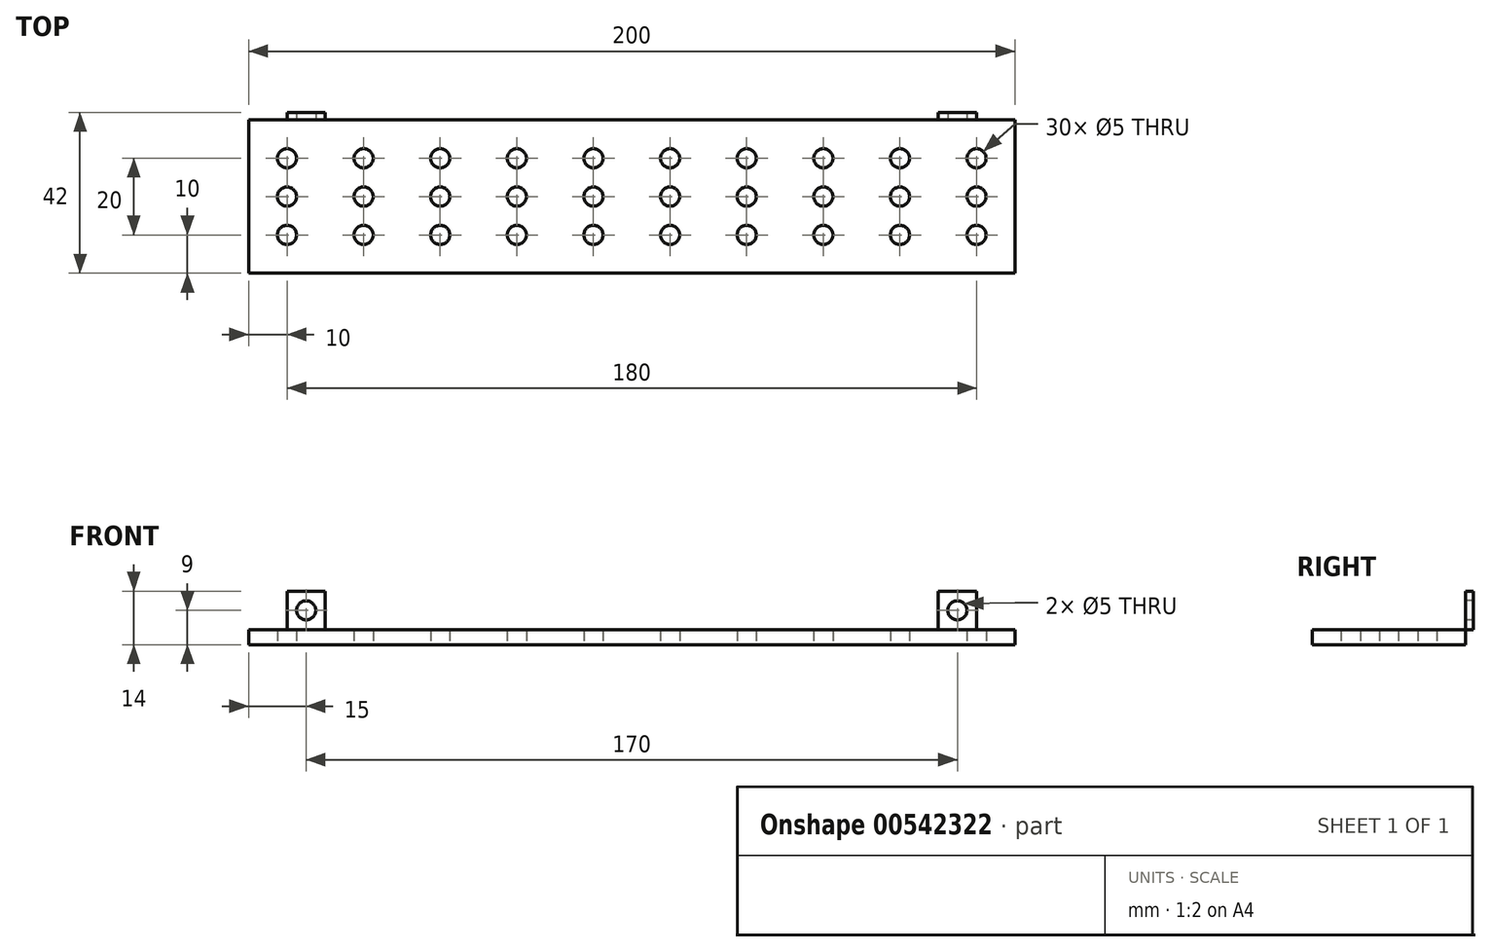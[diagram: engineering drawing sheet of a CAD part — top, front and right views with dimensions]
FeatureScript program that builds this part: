
annotation { "Feature Type Name" : "Feature", "Feature Type Description" : "" }
export const myFeature = defineFeature(function(context is Context, id is Id, definition is map)
    precondition{}
    {
        {
            var Q0;
            Q0=qCreatedBy(makeId("Top.planeOp"),FACE);
            var sketch = newSketch(context, id + "F0", { "sketchPlane" : qUnion([Q0])});
            skLineSegment(sketch, "E0.bottom", {"start": v(100, -20) * mm, "end": v(-100, -20) * mm});
            skLineSegment(sketch, "E0.top", {"start": v(100, 20) * mm, "end": v(-100, 20) * mm});
            skLineSegment(sketch, "E0.left", {"start": v(100, -20) * mm, "end": v(100, 20) * mm});
            skLineSegment(sketch, "E0.right", {"start": v(-100, -20) * mm, "end": v(-100, 20) * mm});
            skPoint(sketch, "E0.middle", {"position": v(0, 0) * mm});
            skCircle(sketch, "E1", {"center": v(-90, 10) * mm, "radius": 2.5 * mm});
            skCircle(sketch, "E2.0.1.0", {"center": v(-90, 0) * mm, "radius": 2.5 * mm});
            skCircle(sketch, "E2.0.2.0", {"center": v(-90, -10) * mm, "radius": 2.5 * mm});
            skCircle(sketch, "E2.1.0.0", {"center": v(-70, 10) * mm, "radius": 2.5 * mm});
            skCircle(sketch, "E2.1.1.0", {"center": v(-70, 0) * mm, "radius": 2.5 * mm});
            skCircle(sketch, "E2.1.2.0", {"center": v(-70, -10) * mm, "radius": 2.5 * mm});
            skCircle(sketch, "E2.2.0.0", {"center": v(-50, 10) * mm, "radius": 2.5 * mm});
            skCircle(sketch, "E2.2.1.0", {"center": v(-50, 0) * mm, "radius": 2.5 * mm});
            skCircle(sketch, "E2.2.2.0", {"center": v(-50, -10) * mm, "radius": 2.5 * mm});
            skCircle(sketch, "E2.3.0.0", {"center": v(-30, 10) * mm, "radius": 2.5 * mm});
            skCircle(sketch, "E2.3.1.0", {"center": v(-30, 0) * mm, "radius": 2.5 * mm});
            skCircle(sketch, "E2.3.2.0", {"center": v(-30, -10) * mm, "radius": 2.5 * mm});
            skCircle(sketch, "E2.4.0.0", {"center": v(-10, 10) * mm, "radius": 2.5 * mm});
            skCircle(sketch, "E2.4.1.0", {"center": v(-10, 0) * mm, "radius": 2.5 * mm});
            skCircle(sketch, "E2.4.2.0", {"center": v(-10, -10) * mm, "radius": 2.5 * mm});
            skCircle(sketch, "E2.5.0.0", {"center": v(10, 10) * mm, "radius": 2.5 * mm});
            skCircle(sketch, "E2.5.1.0", {"center": v(10, 0) * mm, "radius": 2.5 * mm});
            skCircle(sketch, "E2.5.2.0", {"center": v(10, -10) * mm, "radius": 2.5 * mm});
            skCircle(sketch, "E2.6.0.0", {"center": v(30, 10) * mm, "radius": 2.5 * mm});
            skCircle(sketch, "E2.6.1.0", {"center": v(30, 0) * mm, "radius": 2.5 * mm});
            skCircle(sketch, "E2.6.2.0", {"center": v(30, -10) * mm, "radius": 2.5 * mm});
            skCircle(sketch, "E2.7.0.0", {"center": v(50, 10) * mm, "radius": 2.5 * mm});
            skCircle(sketch, "E2.7.1.0", {"center": v(50, 0) * mm, "radius": 2.5 * mm});
            skCircle(sketch, "E2.7.2.0", {"center": v(50, -10) * mm, "radius": 2.5 * mm});
            skCircle(sketch, "E2.8.0.0", {"center": v(70, 10) * mm, "radius": 2.5 * mm});
            skCircle(sketch, "E2.8.1.0", {"center": v(70, 0) * mm, "radius": 2.5 * mm});
            skCircle(sketch, "E2.8.2.0", {"center": v(70, -10) * mm, "radius": 2.5 * mm});
            skCircle(sketch, "E2.9.0.0", {"center": v(90, 10) * mm, "radius": 2.5 * mm});
            skCircle(sketch, "E2.9.1.0", {"center": v(90, 0) * mm, "radius": 2.5 * mm});
            skCircle(sketch, "E2.9.2.0", {"center": v(90, -10) * mm, "radius": 2.5 * mm});
            skLineSegment(sketch, "E2.direction1", {"start": v(-90, 10) * mm, "end": v(-70, 10) * mm, "construction": true});
            skLineSegment(sketch, "E2.direction2", {"start": v(-90, 10) * mm, "end": v(-90, 0) * mm, "construction": true});
            skSolve(sketch);
        }
        {
            var Q0;
            Q0 = qSketchRegion(id + "F0", true);
            extrude(context, id + "F1", {"entities" : qUnion([Q0]), "depth" : 4 * mm, "offsetDistance" : 25 * mm});
        }
        {
            var Q0;
            Q0=makeQuery(id+"F1.opExtrude","SWEPT_FACE",FACE,{"disambiguationData":[OSD([sQuery(id+"F0.wireOp",EDGE,"E0.top")])]});
            var sketch = newSketch(context, id + "F2", { "sketchPlane" : qUnion([Q0])});
            skLineSegment(sketch, "E3.bottom", {"start": v(90, 4) * mm, "end": v(80, 4) * mm});
            skLineSegment(sketch, "E3.top", {"start": v(90, 14) * mm, "end": v(80, 14) * mm});
            skLineSegment(sketch, "E3.left", {"start": v(90, 4) * mm, "end": v(90, 14) * mm});
            skLineSegment(sketch, "E3.right", {"start": v(80, 4) * mm, "end": v(80, 14) * mm});
            skCircle(sketch, "E4", {"center": v(85, 9) * mm, "radius": 2.5 * mm});
            skPoint(sketch, "E4.centerSnap0", {"position": v(90, 9) * mm});
            skPoint(sketch, "E4.centerSnap1", {"position": v(85, 14) * mm});
            skLineSegment(sketch, "E5.MirrorCS", {"start": v(-80, 4) * mm, "end": v(-80, 14) * mm});
            skLineSegment(sketch, "E6.MirrorCS", {"start": v(-90, 14) * mm, "end": v(-80, 14) * mm});
            skLineSegment(sketch, "E7.MirrorCS", {"start": v(-90, 4) * mm, "end": v(-90, 14) * mm});
            skLineSegment(sketch, "E8.MirrorCS", {"start": v(-90, 4) * mm, "end": v(-80, 4) * mm});
            skCircle(sketch, "E9.MirrorC", {"center": v(-85, 9) * mm, "radius": 2.5 * mm});
            skSolve(sketch);
        }
        {
            var Q0;
            Q0 = qSketchRegion(id + "F2", true);
            extrude(context, id + "F3", {"entities" : qUnion([Q0]), "depth" : 2 * mm, "offsetDistance" : 25 * mm});
        }
    });
